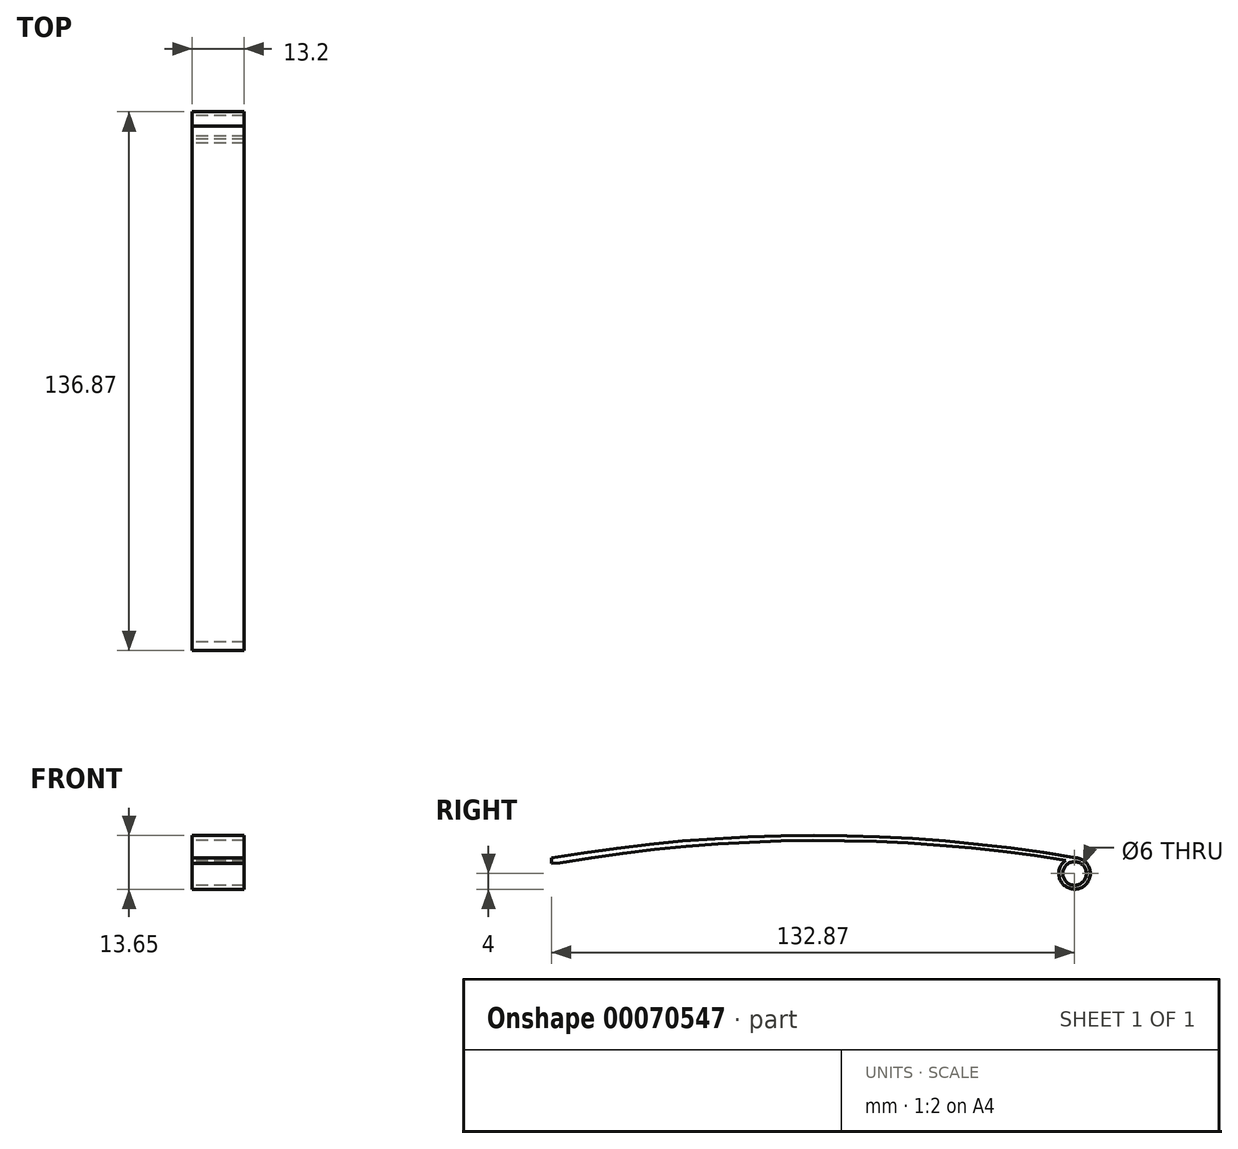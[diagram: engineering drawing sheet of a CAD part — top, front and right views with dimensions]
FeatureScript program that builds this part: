
annotation { "Feature Type Name" : "Feature", "Feature Type Description" : "" }
export const myFeature = defineFeature(function(context is Context, id is Id, definition is map)
    precondition{}
    {
        {
            var Q0;
            Q0=qCreatedBy(makeId("Right.planeOp"),FACE);
            var sketch = newSketch(context, id + "F0", { "sketchPlane" : qUnion([Q0])});
            skLineSegment(sketch, "E0", {"start": v(0, 91.73) * mm, "end": v(0, -64.65) * mm, "construction": true});
            skCircle(sketch, "E1.MirrorC", {"center": v(66, 0) * mm, "radius": 4 * mm});
            skCircle(sketch, "E2.MirrorC", {"center": v(66, 0) * mm, "radius": 3 * mm});
            skArc(sketch, "E3", {"start": v(66, 3) * mm, "mid": v(0.63, 8.34) * mm, "end": v(-64.71, 2.7) * mm});
            skArc(sketch, "E4", {"start": v(66.95, 3.88) * mm, "mid": v(0.04, 9.65) * mm, "end": v(-66.87, 3.9) * mm});
            skLineSegment(sketch, "E5", {"start": v(-66.87, 3.9) * mm, "end": v(-66.87, 2.51) * mm});
            skLineSegment(sketch, "E6", {"start": v(-64.71, 2.7) * mm, "end": v(-66.87, 2.51) * mm});
            skSolve(sketch);
        }
        {
            var Q0;
            Q0 = qSketchRegion(id + "F0", true);
            extrude(context, id + "F1", {"entities" : qUnion([Q0]), "depth" : 13.2 * mm});
        }
    });
